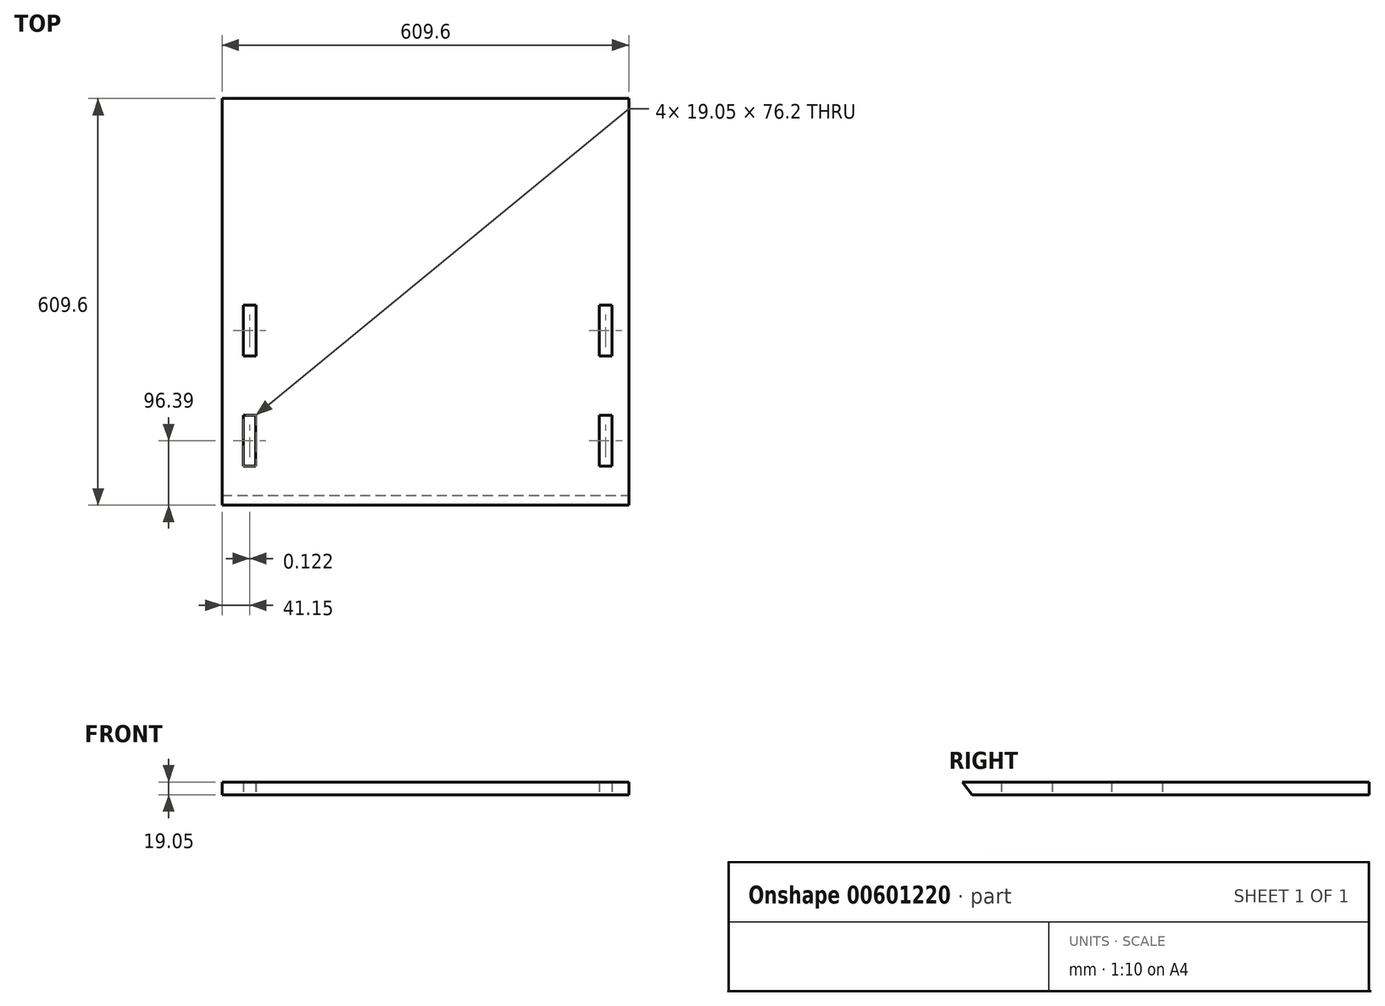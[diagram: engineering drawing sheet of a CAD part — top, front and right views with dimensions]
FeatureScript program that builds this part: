
annotation { "Feature Type Name" : "Feature", "Feature Type Description" : "" }
export const myFeature = defineFeature(function(context is Context, id is Id, definition is map)
    precondition{}
    {
        {
            var Q0;
            Q0=qCreatedBy(makeId("Top.planeOp"),FACE);
            var sketch = newSketch(context, id + "F0", { "sketchPlane" : qUnion([Q0])});
            skLineSegment(sketch, "E0.bottom", {"start": v(-541.72, 150.85) * mm, "end": v(67.88, 150.85) * mm});
            skLineSegment(sketch, "E0.top", {"start": v(-541.72, -458.75) * mm, "end": v(67.88, -458.75) * mm});
            skLineSegment(sketch, "E0.left", {"start": v(-541.72, 150.85) * mm, "end": v(-541.72, -458.75) * mm});
            skLineSegment(sketch, "E0.right", {"start": v(67.88, 150.85) * mm, "end": v(67.88, -458.75) * mm});
            skSolve(sketch);
        }
        {
            var Q0;
            Q0=makeQuery(id+"F0.imprint","IMPRINT",FACE,{"disambiguationData":[TD([[makeQuery(id+"F0.imprint","IMPRINT",EDGE,{"derivedFrom":sQuery(id+"F0.wireOp",EDGE,"E0.bottom")}),-1.0]])]});
            extrude(context, id + "F1", {"entities" : qUnion([Q0]), "depth" : 19.05 * mm, "offsetDistance" : 25.4 * mm});
        }
        {
            var Q0;
            Q0=makeQuery(id+"F1.opExtrude","CAP_FACE",FACE,{"disambiguationData":[OSD([sQuery(id+"F0.wireOp",EDGE,"E0.bottom"),sQuery(id+"F0.wireOp",EDGE,"E0.top"),sQuery(id+"F0.wireOp",EDGE,"E0.left"),sQuery(id+"F0.wireOp",EDGE,"E0.right")])],"isStart":true});
            var sketch = newSketch(context, id + "F2", { "sketchPlane" : qUnion([Q0])});
            skLineSegment(sketch, "E1.MirrorCS", {"start": v(67.88, 39.65) * mm, "end": v(-516.32, 39.65) * mm});
            skLineSegment(sketch, "E2", {"start": v(-516.32, 39.65) * mm, "end": v(-541.72, 39.65) * mm});
            skLineSegment(sketch, "E3", {"start": v(-224.22, 39.65) * mm, "end": v(-224.22, 458.75) * mm});
            skLineSegment(sketch, "E4", {"start": v(-510.1, 324.26) * mm, "end": v(-510.1, 400.46) * mm});
            skLineSegment(sketch, "E5", {"start": v(-510.1, 324.26) * mm, "end": v(-491.05, 324.26) * mm});
            skLineSegment(sketch, "E6", {"start": v(-491.05, 324.26) * mm, "end": v(-491.05, 400.46) * mm});
            skLineSegment(sketch, "E7", {"start": v(-491.05, 400.46) * mm, "end": v(-510.1, 400.46) * mm});
            skLineSegment(sketch, "E8", {"start": v(-509.97, 159.16) * mm, "end": v(-509.97, 235.36) * mm});
            skLineSegment(sketch, "E9", {"start": v(-509.97, 159.16) * mm, "end": v(-490.92, 159.16) * mm});
            skLineSegment(sketch, "E10", {"start": v(-490.92, 159.16) * mm, "end": v(-490.92, 235.36) * mm});
            skLineSegment(sketch, "E11", {"start": v(-490.92, 235.36) * mm, "end": v(-509.97, 235.36) * mm});
            skLineSegment(sketch, "E12.MirrorCS", {"start": v(42.48, 159.16) * mm, "end": v(42.48, 235.36) * mm});
            skLineSegment(sketch, "E13.MirrorCS", {"start": v(42.6, 324.26) * mm, "end": v(42.6, 400.46) * mm});
            skLineSegment(sketch, "E14", {"start": v(42.48, 159.16) * mm, "end": v(23.43, 159.16) * mm});
            skLineSegment(sketch, "E15", {"start": v(23.43, 159.16) * mm, "end": v(23.43, 235.36) * mm});
            skLineSegment(sketch, "E16", {"start": v(23.43, 235.36) * mm, "end": v(42.48, 235.36) * mm});
            skLineSegment(sketch, "E17", {"start": v(42.6, 324.26) * mm, "end": v(23.55, 324.26) * mm});
            skLineSegment(sketch, "E18", {"start": v(23.55, 324.26) * mm, "end": v(23.55, 400.46) * mm});
            skLineSegment(sketch, "E19", {"start": v(23.55, 400.46) * mm, "end": v(42.6, 400.46) * mm});
            skSolve(sketch);
        }
        {
            var Q0;
            {var subQ0=sQuery(id+"F0.wireOp",EDGE,"E0.right");var subQ2=sQuery(id+"F0.wireOp",EDGE,"E0.top");Q0=makeQuery(id+"FrRxhIJtQpzr14x_1.boolean.opBoolean","SPLIT",FACE,{"disambiguationData":[TD([makeQuery(id+"F1.opExtrude","SWEPT_FACE",FACE,{"disambiguationData":[OSD([subQ2])]})])],"derivedFrom":makeQuery(id+"F1.opExtrude","SWEPT_FACE",FACE,{"disambiguationData":[OSD([subQ0])]})});}
            var sketch = newSketch(context, id + "F3", { "sketchPlane" : qUnion([Q0])});
            skLineSegment(sketch, "E20", {"start": v(-458.75, 19.05) * mm, "end": v(-444.02, 0) * mm});
            skSolve(sketch);
        }
        {
            var Q0;
            {var subQ0=sQuery(id+"F3.wireOp",EDGE,"E20");Q0=makeQuery(id+"F3.imprint","IMPRINT",FACE,{"disambiguationData":[TD([[makeQuery(id+"F3.imprint","IMPRINT",EDGE,{"derivedFrom":subQ0}),-1.0]])]});}
            extrude(context, id + "F4", {"entities" : qUnion([Q0]), "operationType" : NewBodyOperationType.REMOVE, "oppositeDirection" : true, "depth" : 747 * mm, "offsetDistance" : 25.4 * mm});
        }
        {
            var Q0;
            Q0 = qSketchRegion(id + "F2", true);
            extrude(context, id + "F5", {"entities" : qUnion([Q0]), "operationType" : NewBodyOperationType.REMOVE, "oppositeDirection" : true, "depth" : 25.4 * mm, "offsetDistance" : 25.4 * mm});
        }
    });
